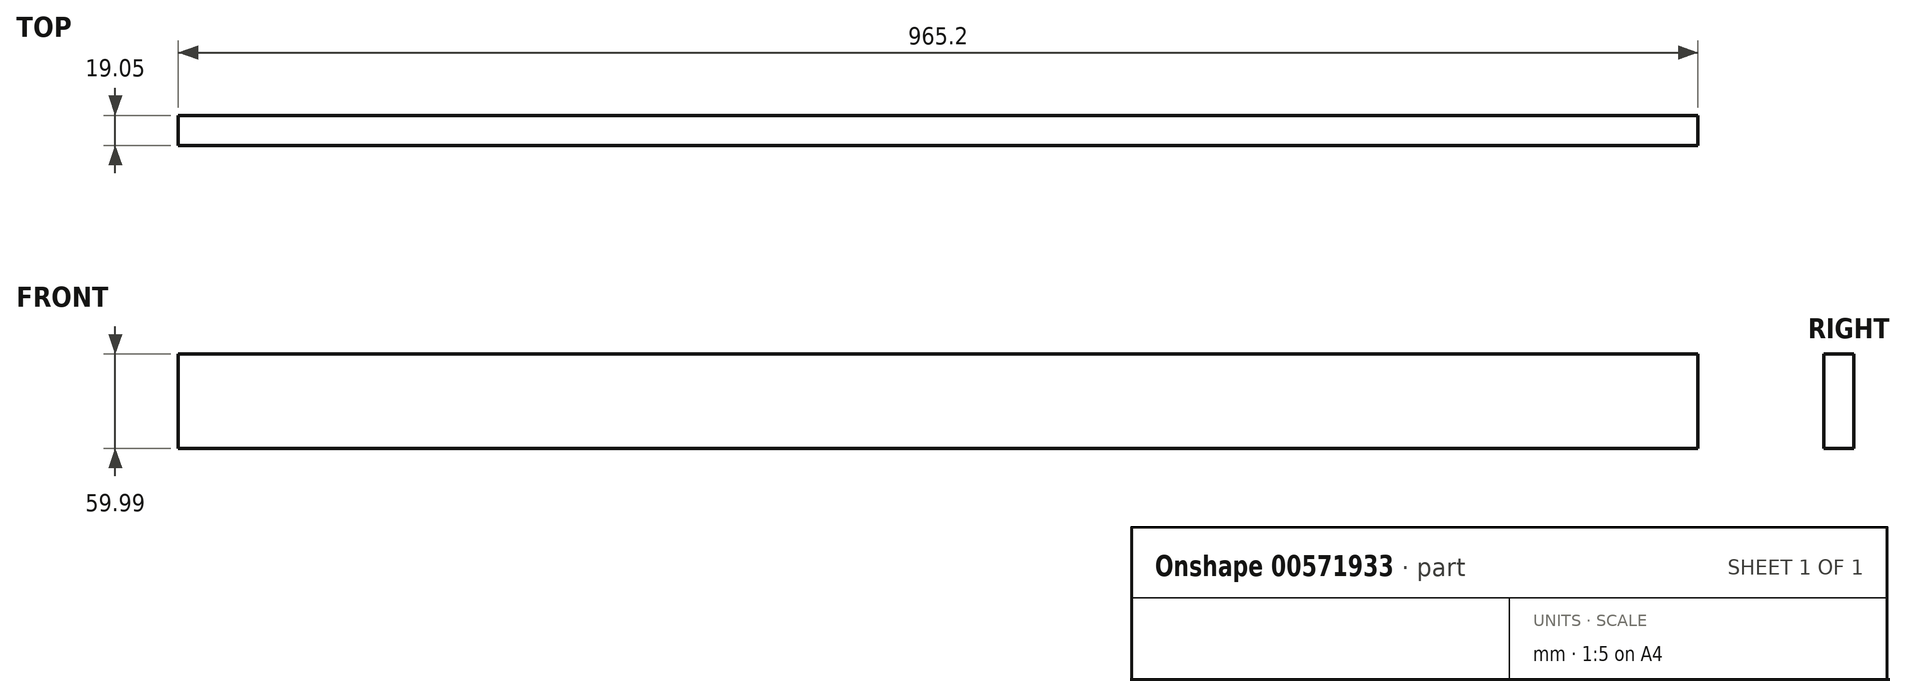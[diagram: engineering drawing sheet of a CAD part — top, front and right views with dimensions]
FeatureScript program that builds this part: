
annotation { "Feature Type Name" : "Feature", "Feature Type Description" : "" }
export const myFeature = defineFeature(function(context is Context, id is Id, definition is map)
    precondition{}
    {
        {
            var Q0;
            Q0=qCreatedBy(makeId("Top.planeOp"),FACE);
            var sketch = newSketch(context, id + "F0", { "sketchPlane" : qUnion([Q0])});
            skLineSegment(sketch, "E0", {"start": v(488, 0) * mm, "end": v(-477.2, 0) * mm});
            skLineSegment(sketch, "E1", {"start": v(-477.2, 0) * mm, "end": v(-477.2, 19.05) * mm});
            skLineSegment(sketch, "E2", {"start": v(-477.2, 19.05) * mm, "end": v(488, 19.05) * mm});
            skLineSegment(sketch, "E3", {"start": v(488, 19.05) * mm, "end": v(488, 0) * mm});
            skSolve(sketch);
        }
        {
            var Q0;
            Q0 = qSketchRegion(id + "F0", true);
            extrude(context, id + "F1", {"entities" : qUnion([Q0]), "depth" : 60 * mm, "offsetDistance" : 25.4 * mm});
        }
    });
